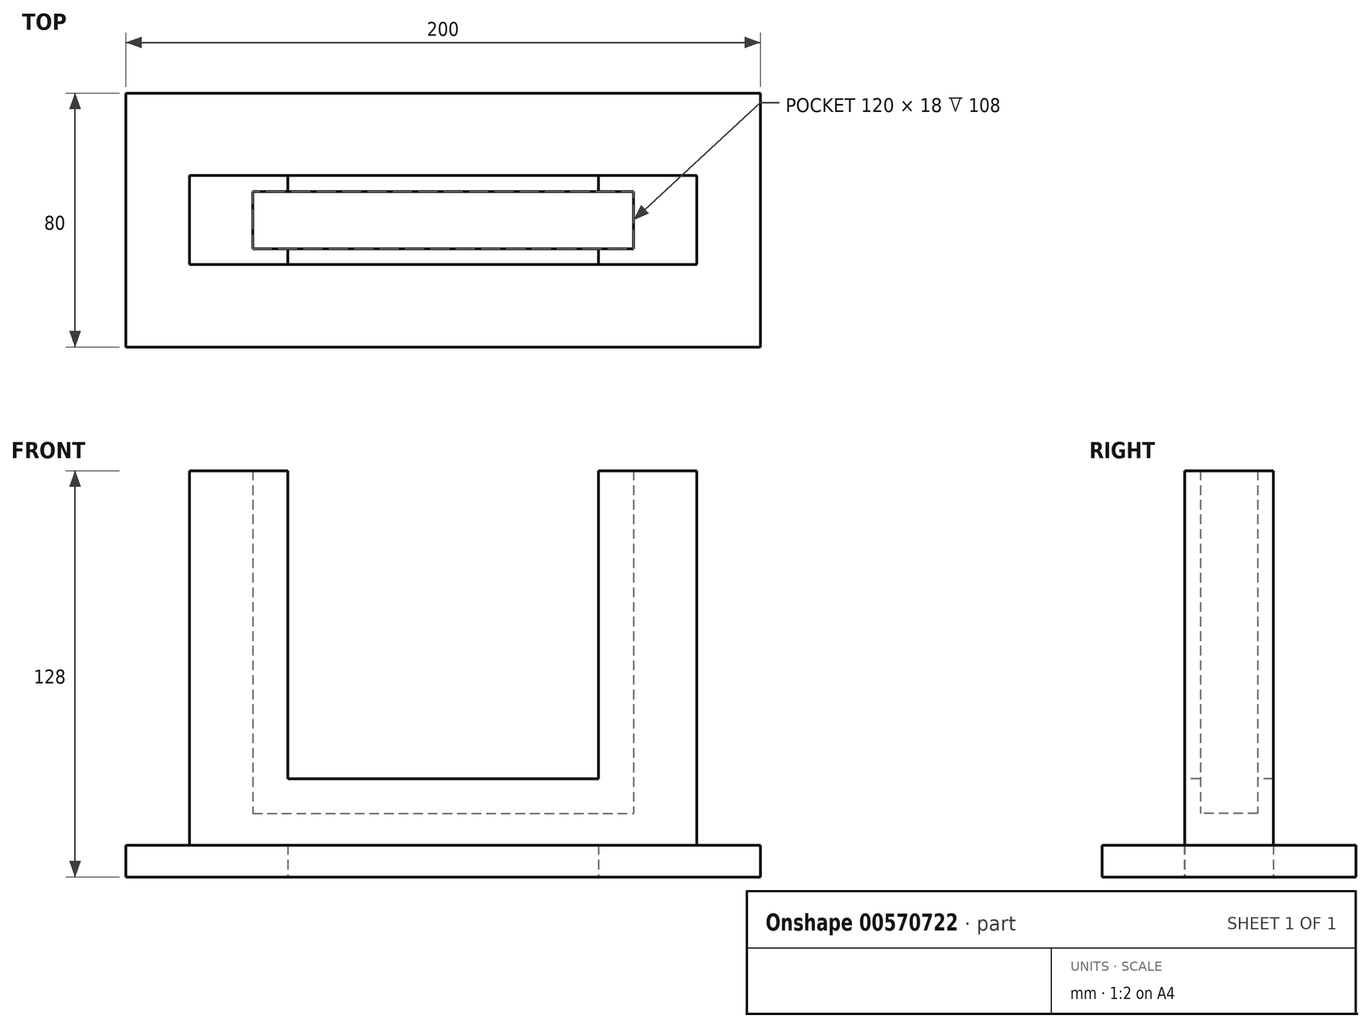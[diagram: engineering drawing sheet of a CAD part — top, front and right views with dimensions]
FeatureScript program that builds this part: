
annotation { "Feature Type Name" : "Feature", "Feature Type Description" : "" }
export const myFeature = defineFeature(function(context is Context, id is Id, definition is map)
    precondition{}
    {
        {
            var Q0;
            Q0=qCreatedBy(makeId("Top.planeOp"),FACE);
            var sketch = newSketch(context, id + "F0", { "sketchPlane" : qUnion([Q0])});
            skLineSegment(sketch, "E0.bottom", {"start": v(80, -14) * mm, "end": v(-80, -14) * mm});
            skLineSegment(sketch, "E0.top", {"start": v(80, 14) * mm, "end": v(-80, 14) * mm});
            skLineSegment(sketch, "E0.left", {"start": v(80, -14) * mm, "end": v(80, 14) * mm});
            skLineSegment(sketch, "E0.right", {"start": v(-80, -14) * mm, "end": v(-80, 14) * mm});
            skPoint(sketch, "E0.middle", {"position": v(0, 0) * mm});
            skLineSegment(sketch, "E1.bottom", {"start": v(60, -9) * mm, "end": v(-60, -9) * mm});
            skLineSegment(sketch, "E1.top", {"start": v(60, 9) * mm, "end": v(-60, 9) * mm});
            skLineSegment(sketch, "E1.left", {"start": v(60, -9) * mm, "end": v(60, 9) * mm});
            skLineSegment(sketch, "E1.right", {"start": v(-60, -9) * mm, "end": v(-60, 9) * mm});
            skLineSegment(sketch, "E2.bottom", {"start": v(100, -40) * mm, "end": v(-100, -40) * mm});
            skLineSegment(sketch, "E2.top", {"start": v(100, 40) * mm, "end": v(-100, 40) * mm});
            skLineSegment(sketch, "E2.left", {"start": v(100, -40) * mm, "end": v(100, 40) * mm});
            skLineSegment(sketch, "E2.right", {"start": v(-100, -40) * mm, "end": v(-100, 40) * mm});
            skLineSegment(sketch, "E3.bottom", {"start": v(49, -14.05) * mm, "end": v(-49, -14.05) * mm});
            skLineSegment(sketch, "E3.top", {"start": v(49, 14.05) * mm, "end": v(-49, 14.05) * mm});
            skLineSegment(sketch, "E3.left", {"start": v(49, -14.05) * mm, "end": v(49, 14.05) * mm});
            skLineSegment(sketch, "E3.right", {"start": v(-49, -14.05) * mm, "end": v(-49, 14.05) * mm});
            skSolve(sketch);
        }
        {
            var Q0;
            Q0=makeQuery(id+"F0.imprint","IMPRINT",FACE,{"disambiguationData":[TD([[makeQuery(id+"F0.imprint","IMPRINT",EDGE,{"derivedFrom":sQuery(id+"F0.wireOp",EDGE,"E0.bottom")}),-1.0]])]});
            var Q1;
            Q1=makeQuery(id+"F0.imprint","IMPRINT",FACE,{"disambiguationData":[TD([[makeQuery(id+"F0.imprint","IMPRINT",EDGE,{"derivedFrom":sQuery(id+"F0.wireOp",EDGE,"E1.bottom")}),-1.0]])]});
            var Q2;
            Q2=makeQuery(id+"F0.imprint","IMPRINT",FACE,{"disambiguationData":[TD([[makeQuery(id+"F0.imprint","IMPRINT",EDGE,{"derivedFrom":sQuery(id+"F0.wireOp",EDGE,"P9HjnNf5-5k27-Fy6A-rmzK-eQZUQiiEZai5.bottom")}),-1.0]])]});
            var Q3;
            Q3=makeQuery(id+"F0.imprint","IMPRINT",FACE,{"disambiguationData":[TD([[makeQuery(id+"F0.imprint","IMPRINT",EDGE,{"derivedFrom":sQuery(id+"F0.wireOp",EDGE,"E0.bottom")}),1.0]])]});
            var Q4;
            {var subQ4=sQuery(id+"F0.wireOp",EDGE,"E0.right");Q4=makeQuery(id+"F0.imprint","IMPRINT",FACE,{"disambiguationData":[TD([[makeQuery(id+"F0.imprint","IMPRINT",EDGE,{"derivedFrom":subQ4}),-1.0]])]});}
            var Q5;
            {var subQ0=sQuery(id+"F0.wireOp",EDGE,"E3.left");var subQ1=sQuery(id+"F0.wireOp",EDGE,"E0.top");var subQ2=makeQuery(id+"F0.imprint","INTERSECT",VERTEX,{"derivedFrom":[subQ1,subQ0]});Q5=makeQuery(id+"F0.imprint","IMPRINT",FACE,{"disambiguationData":[TD([[makeQuery(id+"F0.imprint","IMPRINT",EDGE,{"disambiguationData":[TD([[subQ2,-1.0]])],"derivedFrom":subQ1}),1.0]])]});}
            var Q6;
            {var subQ0=sQuery(id+"F0.wireOp",EDGE,"E0.left");Q6=makeQuery(id+"F0.imprint","IMPRINT",FACE,{"disambiguationData":[TD([[makeQuery(id+"F0.imprint","IMPRINT",EDGE,{"derivedFrom":subQ0}),1.0]])]});}
            extrude(context, id + "F1", {"entities" : qUnion([Q0, Q1, Q2, Q3, Q4, Q5, Q6]), "depth" : 10 * mm, "offsetDistance" : 25 * mm});
        }
        {
            var Q0;
            {var subQ4=sQuery(id+"F0.wireOp",EDGE,"E0.right");Q0=makeQuery(id+"F0.imprint","IMPRINT",FACE,{"disambiguationData":[TD([[makeQuery(id+"F0.imprint","IMPRINT",EDGE,{"derivedFrom":subQ4}),-1.0]])]});}
            var Q1;
            {var subQ0=sQuery(id+"F0.wireOp",EDGE,"E1.right");Q1=makeQuery(id+"F0.imprint","IMPRINT",FACE,{"disambiguationData":[TD([[makeQuery(id+"F0.imprint","IMPRINT",EDGE,{"derivedFrom":subQ0}),-1.0]])]});}
            var Q2;
            {var subQ0=sQuery(id+"F0.wireOp",EDGE,"E3.left");var subQ1=sQuery(id+"F0.wireOp",EDGE,"E1.bottom");var subQ2=makeQuery(id+"F0.imprint","INTERSECT",VERTEX,{"derivedFrom":[subQ1,subQ0]});Q2=makeQuery(id+"F0.imprint","IMPRINT",FACE,{"disambiguationData":[TD([[makeQuery(id+"F0.imprint","IMPRINT",EDGE,{"disambiguationData":[TD([[subQ2,-1.0]])],"derivedFrom":subQ1}),-1.0]])]});}
            var Q3;
            {var subQ0=sQuery(id+"F0.wireOp",EDGE,"E1.left");Q3=makeQuery(id+"F0.imprint","IMPRINT",FACE,{"disambiguationData":[TD([[makeQuery(id+"F0.imprint","IMPRINT",EDGE,{"derivedFrom":subQ0}),1.0]])]});}
            var Q4;
            {var subQ0=sQuery(id+"F0.wireOp",EDGE,"E0.left");Q4=makeQuery(id+"F0.imprint","IMPRINT",FACE,{"disambiguationData":[TD([[makeQuery(id+"F0.imprint","IMPRINT",EDGE,{"derivedFrom":subQ0}),1.0]])]});}
            var Q5;
            {var subQ0=sQuery(id+"F0.wireOp",EDGE,"E3.left");var subQ1=sQuery(id+"F0.wireOp",EDGE,"E0.bottom");var subQ2=makeQuery(id+"F0.imprint","INTERSECT",VERTEX,{"derivedFrom":[subQ1,subQ0]});Q5=makeQuery(id+"F0.imprint","IMPRINT",FACE,{"disambiguationData":[TD([[makeQuery(id+"F0.imprint","IMPRINT",EDGE,{"disambiguationData":[TD([[subQ2,-1.0]])],"derivedFrom":subQ1}),-1.0]])]});}
            var Q6;
            {var subQ0=sQuery(id+"F0.wireOp",EDGE,"E3.left");var subQ1=sQuery(id+"F0.wireOp",EDGE,"E0.top");var subQ2=makeQuery(id+"F0.imprint","INTERSECT",VERTEX,{"derivedFrom":[subQ1,subQ0]});Q6=makeQuery(id+"F0.imprint","IMPRINT",FACE,{"disambiguationData":[TD([[makeQuery(id+"F0.imprint","IMPRINT",EDGE,{"disambiguationData":[TD([[subQ2,-1.0]])],"derivedFrom":subQ1}),1.0]])]});}
            extrude(context, id + "F2", {"entities" : qUnion([Q0, Q1, Q2, Q3, Q4, Q5, Q6]), "operationType" : NewBodyOperationType.ADD, "depth" : 20 * mm, "offsetDistance" : 25 * mm});
        }
        {
            var Q0;
            {var subQ4=sQuery(id+"F0.wireOp",EDGE,"E0.right");Q0=makeQuery(id+"F0.imprint","IMPRINT",FACE,{"disambiguationData":[TD([[makeQuery(id+"F0.imprint","IMPRINT",EDGE,{"derivedFrom":subQ4}),-1.0]])]});}
            var Q1;
            {var subQ0=sQuery(id+"F0.wireOp",EDGE,"E3.left");var subQ1=sQuery(id+"F0.wireOp",EDGE,"E0.top");var subQ2=makeQuery(id+"F0.imprint","INTERSECT",VERTEX,{"derivedFrom":[subQ1,subQ0]});Q1=makeQuery(id+"F0.imprint","IMPRINT",FACE,{"disambiguationData":[TD([[makeQuery(id+"F0.imprint","IMPRINT",EDGE,{"disambiguationData":[TD([[subQ2,-1.0]])],"derivedFrom":subQ1}),1.0]])]});}
            var Q2;
            {var subQ0=sQuery(id+"F0.wireOp",EDGE,"E3.left");var subQ1=sQuery(id+"F0.wireOp",EDGE,"E0.bottom");var subQ2=makeQuery(id+"F0.imprint","INTERSECT",VERTEX,{"derivedFrom":[subQ1,subQ0]});Q2=makeQuery(id+"F0.imprint","IMPRINT",FACE,{"disambiguationData":[TD([[makeQuery(id+"F0.imprint","IMPRINT",EDGE,{"disambiguationData":[TD([[subQ2,-1.0]])],"derivedFrom":subQ1}),-1.0]])]});}
            var Q3;
            {var subQ0=sQuery(id+"F0.wireOp",EDGE,"E0.left");Q3=makeQuery(id+"F0.imprint","IMPRINT",FACE,{"disambiguationData":[TD([[makeQuery(id+"F0.imprint","IMPRINT",EDGE,{"derivedFrom":subQ0}),1.0]])]});}
            extrude(context, id + "F3", {"entities" : qUnion([Q0, Q1, Q2, Q3]), "operationType" : NewBodyOperationType.ADD, "depth" : 31 * mm, "offsetDistance" : 25 * mm});
        }
        {
            var Q0;
            {var subQ4=sQuery(id+"F0.wireOp",EDGE,"E0.right");Q0=makeQuery(id+"F0.imprint","IMPRINT",FACE,{"disambiguationData":[TD([[makeQuery(id+"F0.imprint","IMPRINT",EDGE,{"derivedFrom":subQ4}),-1.0]])]});}
            var Q1;
            {var subQ0=sQuery(id+"F0.wireOp",EDGE,"E0.left");Q1=makeQuery(id+"F0.imprint","IMPRINT",FACE,{"disambiguationData":[TD([[makeQuery(id+"F0.imprint","IMPRINT",EDGE,{"derivedFrom":subQ0}),1.0]])]});}
            extrude(context, id + "F4", {"entities" : qUnion([Q0, Q1]), "operationType" : NewBodyOperationType.ADD, "depth" : 128 * mm, "offsetDistance" : 25 * mm});
        }
    });
